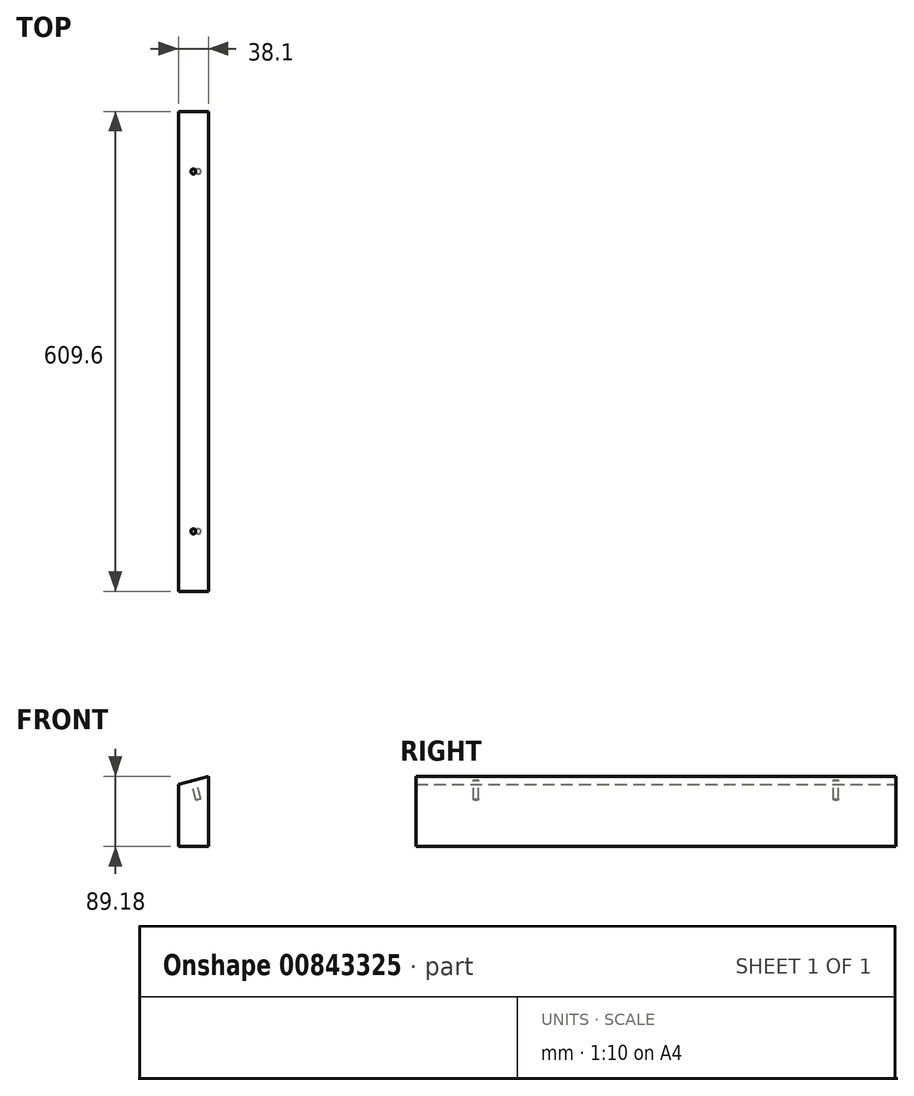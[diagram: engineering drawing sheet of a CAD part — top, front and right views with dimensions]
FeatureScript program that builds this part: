
annotation { "Feature Type Name" : "Feature", "Feature Type Description" : "" }
export const myFeature = defineFeature(function(context is Context, id is Id, definition is map)
    precondition{}
    {
        {
            var Q0;
            Q0=qCreatedBy(makeId("Front.planeOp"),FACE);
            var sketch = newSketch(context, id + "F0", { "sketchPlane" : qUnion([Q0])});
            skLineSegment(sketch, "E0", {"start": v(19.05, -44.45) * mm, "end": v(19.05, 44.45) * mm});
            skLineSegment(sketch, "E1", {"start": v(19.05, 44.45) * mm, "end": v(-19.05, 34.24) * mm});
            skLineSegment(sketch, "E2", {"start": v(-19.05, 34.24) * mm, "end": v(-19.05, -44.73) * mm});
            skLineSegment(sketch, "E3", {"start": v(-19.05, -44.73) * mm, "end": v(19.05, -44.45) * mm});
            skSolve(sketch);
        }
        {
            var Q0;
            Q0 = qSketchRegion(id + "F0", true);
            extrude(context, id + "F1", {"entities" : qUnion([Q0]), "depth" : 609.6 * mm, "offsetDistance" : 25.4 * mm});
        }
        {
            var Q0;
            Q0=makeQuery(id+"F1.opExtrude","SWEPT_FACE",FACE,{"disambiguationData":[OSD([sQuery(id+"F0.wireOp",EDGE,"E1")])]});
            var sketch = newSketch(context, id + "F2", { "sketchPlane" : qUnion([Q0])});
            skLineSegment(sketch, "E4", {"start": v(10.18, 23.38) * mm, "end": v(10.18, -643.83) * mm, "construction": true});
            skSolve(sketch);
        }
        {
            var Q0;
            {var subQ0=sQuery(id+"F0.wireOp",EDGE,"E1");Q0=makeQuery(id+"F2.imprint","IMPRINT",FACE,{"disambiguationData":[TD([[makeQuery(id+"F2.imprint","IMPRINT",EDGE,{"derivedFrom":makeQuery(id+"F1.opExtrude","CAP_EDGE",EDGE,{"disambiguationData":[OSD([subQ0])],"isStart":true})}),1.0]])]});}
            var sketch = newSketch(context, id + "F3", { "sketchPlane" : qUnion([Q0])});
            skCircle(sketch, "E5", {"center": v(10.18, -76.2) * mm, "radius": 3.18 * mm});
            skCircle(sketch, "E6", {"center": v(10.18, -533.4) * mm, "radius": 3.18 * mm});
            skSolve(sketch);
        }
        {
            var Q0;
            Q0 = qSketchRegion(id + "F3", true);
            extrude(context, id + "F4", {"entities" : qUnion([Q0]), "operationType" : NewBodyOperationType.REMOVE, "oppositeDirection" : true, "depth" : 25.4 * mm, "offsetDistance" : 25.4 * mm});
        }
    });
